# Revit family: REVIT-300-1500 HST- CONVH
name_source: partatom
category: Mechanical Equipment
revit_build: Autodesk Revit 2017 (Build: 20190507_1515(x64)
units: mm (PartAtom-declared; Revit-internal decimal feet)

## family parameters
Always vertical = Yes
Cut with Voids When Loaded = No
Part Type = Normal
Room Calculation Point = No
Round Connector Dimension = Use Radius
Shared = No
Work Plane-Based = No

## types (9) — shared parameters
Aquaplex = Yes
Assembly Code = D3040400
Circulating NPT = 3"
Circulating Radius = 1 1/2"
Description = PVI AquaPLEX® Storage Tanks - Horizontal Storage Tanks
Disclaimer = This rendering is for building modeling purposes only. Submittal/catalog is still the contract document. PVI reserves the right to change design and specification without notice.
Manufacturer = PVI Industries, LLC
Relief Valve NPT = 1"
Relief Valve Radius = 1/2"
Skid Width = 6"
Temperature Gauge NPT = 3/4"
Temperature Gauge Radius = 3/8"
Thermowell NPT = 3/4"
Thermowell Radius = 3/8"
URL = www.pvi.com

## per-type parameters (varying)
- LH 300A-TR: Circulating Connection Location=16"; Circulating Extension=24"; Circulating Rotate Extension=24"; Cold Water Extension=24"; Cold Water Location=16"; Cold Water NPT=2"; Cold Water Radius=1"; Drain Extension=26"; Drain Location=18"; Drain NPT=1"; Drain Radius=1/2"; Height To Center=31 1/2"; Hot Water Extension=24"; Hot Water NPT=2"; Hot Water Outlet Location=18"; Hot Water Radius=1"; Leg To Center=13 13/32"; Lifting Lug Extension=24 1/4"; Lifting Lug To Front=30"; Lifting Lug To Rear=28"; Nominal Storage=300 gal; Relief Extension=26"; Relief Location=16"; Skid Length=42"; Skid Spacing=30"; Skid To Center=21"; Skid To Rear=21"; Temperature Gauge Extension=24"; Temperature Gauge Location=23 1/4"; Thermowell Location=36"; Unit Height=56"; Unit Length=74"; Unit Radius=23"; Weight=1010
- LH 400A-TR: Circulating Connection Location=16"; Circulating Extension=24"; Circulating Rotate Extension=24"; Cold Water Extension=24"; Cold Water Location=16"; Cold Water NPT=2"; Cold Water Radius=1"; Drain Extension=26"; Drain Location=18"; Drain NPT=1"; Drain Radius=1/2"; Height To Center=31 1/2"; Hot Water Extension=24"; Hot Water NPT=2"; Hot Water Outlet Location=18"; Hot Water Radius=1"; Leg To Center=13 13/32"; Lifting Lug Extension=24 1/4"; Lifting Lug To Front=30"; Lifting Lug To Rear=28"; Nominal Storage=400 gal; Relief Extension=26"; Relief Location=16"; Skid Length=42"; Skid Spacing=42"; Skid To Center=21"; Skid To Rear=21"; Temperature Gauge Extension=24"; Temperature Gauge Location=23 1/4"; Thermowell Location=42"; Unit Height=56"; Unit Length=86"; Unit Radius=23"; Weight=1055
- LH 500A-TR: Circulating Connection Location=18"; Circulating Extension=29"; Circulating Rotate Extension=29"; Cold Water Extension=29"; Cold Water Location=18"; Cold Water NPT=3"; Cold Water Radius=1 1/2"; Drain Extension=31"; Drain Location=19"; Drain NPT=1 1/2"; Drain Radius=3/4"; Height To Center=36"; Hot Water Extension=29"; Hot Water NPT=3"; Hot Water Outlet Location=19"; Hot Water Radius=1 1/2"; Leg To Center=15 3/8"; Lifting Lug Extension=29 1/4"; Lifting Lug To Front=31"; Lifting Lug To Rear=30"; Nominal Storage=500 gal; Relief Extension=31"; Relief Location=18"; Skid Length=52"; Skid Spacing=30"; Skid To Center=26"; Skid To Rear=23"; Temperature Gauge Extension=29"; Temperature Gauge Location=24 1/4"; Thermowell Location=38"; Unit Height=66"; Unit Length=77"; Unit Radius=28"; Weight=1525
- LH 600A-TR: Circulating Connection Location=18"; Circulating Extension=29"; Circulating Rotate Extension=29"; Cold Water Extension=29"; Cold Water Location=18"; Cold Water NPT=3"; Cold Water Radius=1 1/2"; Drain Extension=31"; Drain Location=19"; Drain NPT=1 1/2"; Drain Radius=3/4"; Height To Center=36"; Hot Water Extension=29"; Hot Water NPT=3"; Hot Water Outlet Location=19"; Hot Water Radius=1 1/2"; Leg To Center=15 3/8"; Lifting Lug Extension=29 1/4"; Lifting Lug To Front=31"; Lifting Lug To Rear=30"; Nominal Storage=600 gal; Relief Extension=31"; Relief Location=18"; Skid Length=52"; Skid Spacing=42"; Skid To Center=26"; Skid To Rear=23"; Temperature Gauge Extension=29"; Temperature Gauge Location=24 1/4"; Thermowell Location=44"; Unit Height=66"; Unit Length=89"; Unit Radius=28"; Weight=1685
- LH 750A-TR: Circulating Connection Location=20"; Circulating Extension=34 1/2"; Circulating Rotate Extension=34 1/2"; Cold Water Extension=34 1/2"; Cold Water Location=20"; Cold Water NPT=3"; Cold Water Radius=1 1/2"; Drain Extension=36 1/2"; Drain Location=22"; Drain NPT=1 1/2"; Drain Radius=3/4"; Height To Center=40 1/2"; Hot Water Extension=34 1/2"; Hot Water NPT=3"; Hot Water Outlet Location=22"; Hot Water Radius=1 1/2"; Leg To Center=25 1/4"; Lifting Lug Extension=34 3/4"; Lifting Lug To Front=34"; Lifting Lug To Rear=32"; Nominal Storage=750 gal; Relief Extension=36 1/2"; Relief Location=20"; Skid Length=64"; Skid Spacing=30"; Skid To Center=32"; Skid To Rear=25"; Temperature Gauge Extension=34 1/2"; Temperature Gauge Location=27 1/4"; Thermowell Location=40"; Unit Height=77"; Unit Length=82"; Unit Radius=33 1/2"; Weight=2180
- LH 1000A-TR: Circulating Connection Location=20"; Circulating Extension=34 1/2"; Circulating Rotate Extension=34 1/2"; Cold Water Extension=34 1/2"; Cold Water Location=20"; Cold Water NPT=3"; Cold Water Radius=1 1/2"; Drain Extension=36 1/2"; Drain Location=22"; Drain NPT=1 1/2"; Drain Radius=3/4"; Height To Center=40 1/2"; Hot Water Extension=34 1/2"; Hot Water NPT=3"; Hot Water Outlet Location=22"; Hot Water Radius=1 1/2"; Leg To Center=25 1/4"; Lifting Lug Extension=34 3/4"; Lifting Lug To Front=34"; Lifting Lug To Rear=32"; Nominal Storage=1000 gal; Relief Extension=36 1/2"; Relief Location=20"; Skid Length=64"; Skid Spacing=54"; Skid To Center=32"; Skid To Rear=25"; Temperature Gauge Extension=34 1/2"; Temperature Gauge Location=27 1/4"; Thermowell Location=52"; Unit Height=77"; Unit Length=106"; Unit Radius=33 1/2"; Weight=2645
- LH 1250A-TR: Circulating Connection Location=21"; Circulating Extension=38 1/2"; Circulating Rotate Extension=38 1/2"; Cold Water Extension=38 1/2"; Cold Water Location=21"; Cold Water NPT=3"; Cold Water Radius=1 1/2"; Drain Extension=40 1/2"; Drain Location=23"; Drain NPT=2"; Drain Radius=1"; Height To Center=46 1/2"; Hot Water Extension=38 1/2"; Hot Water NPT=3"; Hot Water Outlet Location=23"; Hot Water Radius=1 1/2"; Leg To Center=23 3/4"; Lifting Lug Extension=38 3/4"; Lifting Lug To Front=35"; Lifting Lug To Rear=33"; Nominal Storage=1250 gal; Relief Extension=40 1/2"; Relief Location=21"; Skid Length=70"; Skid Spacing=42"; Skid To Center=35"; Skid To Rear=26"; Temperature Gauge Extension=38 1/2"; Temperature Gauge Location=28 1/4"; Thermowell Location=47"; Unit Height=87"; Unit Length=96"; Unit Radius=37 1/2"; Weight=3010
- LH 1500A-TR: Circulating Connection Location=21"; Circulating Extension=38 1/2"; Circulating Rotate Extension=38 1/2"; Cold Water Extension=38 1/2"; Cold Water Location=21"; Cold Water NPT=3"; Cold Water Radius=1 1/2"; Drain Extension=40 1/2"; Drain Location=23"; Drain NPT=2"; Drain Radius=1"; Height To Center=46 1/2"; Hot Water Extension=38 1/2"; Hot Water NPT=3"; Hot Water Outlet Location=23"; Hot Water Radius=1 1/2"; Leg To Center=23 3/4"; Lifting Lug Extension=38 3/4"; Lifting Lug To Front=35"; Lifting Lug To Rear=33"; Nominal Storage=1500 gal; Relief Extension=40 1/2"; Relief Location=21"; Skid Length=70"; Skid Spacing=54"; Skid To Center=35"; Skid To Rear=26"; Temperature Gauge Extension=38 1/2"; Temperature Gauge Location=28 1/4"; Thermowell Location=53"; Unit Height=87"; Unit Length=108"; Unit Radius=37 1/2"; Weight=3245
- LH 900A-TR: Circulating Connection Location=20"; Circulating Extension=34 1/2"; Circulating Rotate Extension=34 1/2"; Cold Water Extension=34 1/2"; Cold Water Location=20"; Cold Water NPT=3"; Cold Water Radius=1 1/2"; Drain Extension=36 1/2"; Drain Location=22"; Drain NPT=1 1/2"; Drain Radius=3/4"; Height To Center=40 1/2"; Hot Water Extension=34 1/2"; Hot Water NPT=3"; Hot Water Outlet Location=22"; Hot Water Radius=1 1/2"; Leg To Center=25 1/4"; Lifting Lug Extension=34 3/4"; Lifting Lug To Front=34"; Lifting Lug To Rear=32"; Nominal Storage=900 gal; Relief Extension=36 1/2"; Relief Location=20"; Skid Length=64"; Skid Spacing=42"; Skid To Center=32"; Skid To Rear=25"; Temperature Gauge Extension=34 1/2"; Temperature Gauge Location=27 1/4"; Thermowell Location=46"; Unit Height=77"; Unit Length=94"; Unit Radius=33 1/2"; Weight=2410

note: column(s) folded — value = type name in every type: Model

## geometry (parser evidence)
native form markers: Sweep x2
no freeform markers — native parametric forms only
